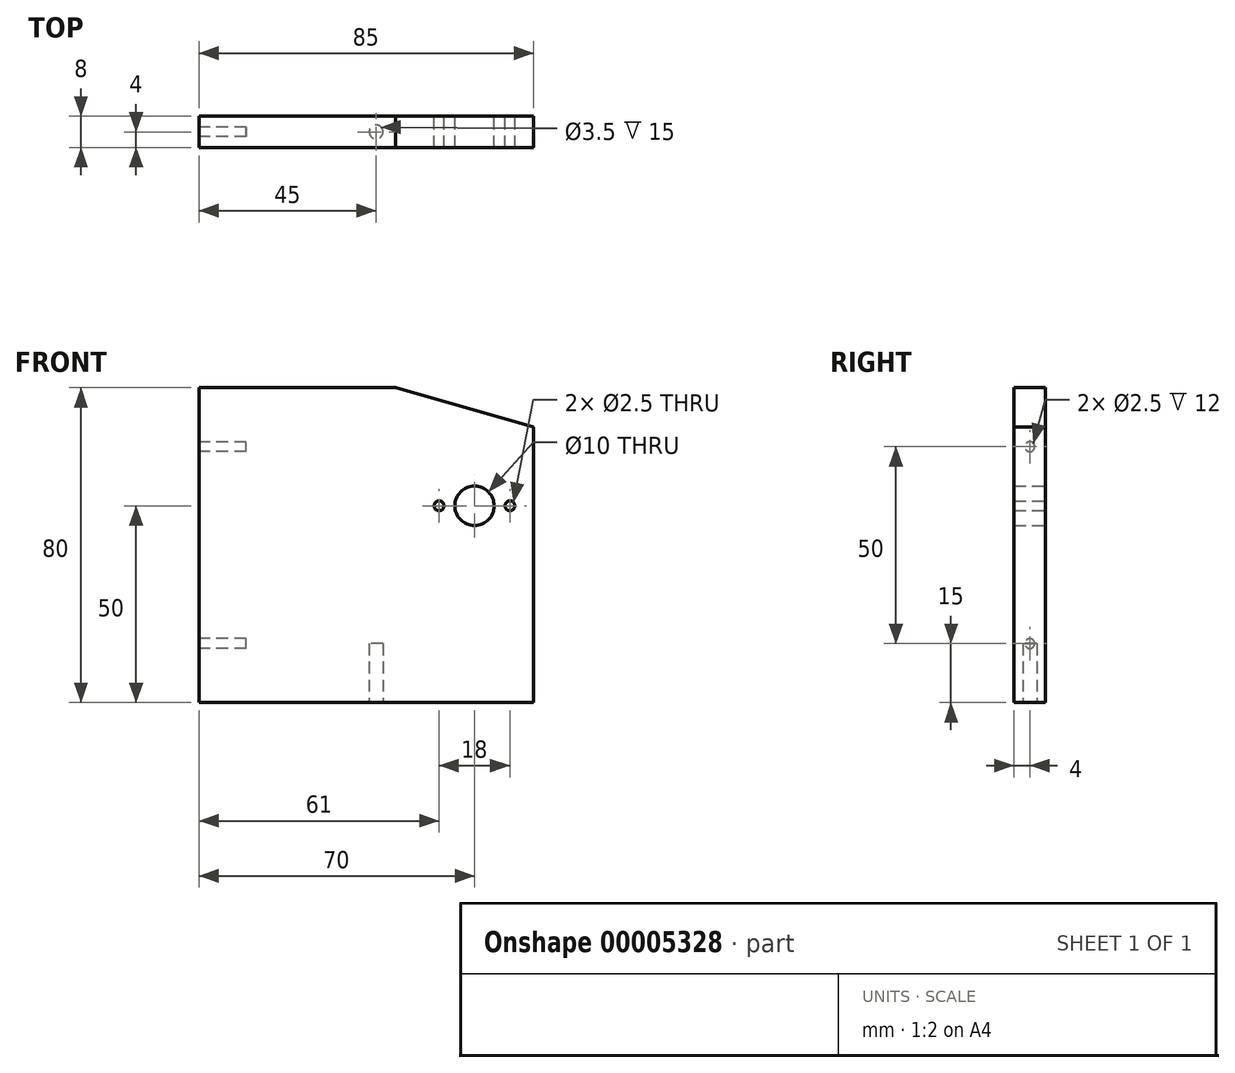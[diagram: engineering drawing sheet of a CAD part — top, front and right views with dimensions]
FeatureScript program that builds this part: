
annotation { "Feature Type Name" : "Feature", "Feature Type Description" : "" }
export const myFeature = defineFeature(function(context is Context, id is Id, definition is map)
    precondition{}
    {
        {
            var Q0;
            Q0=qCreatedBy(makeId("Front.planeOp"),FACE);
            var sketch = newSketch(context, id + "F0", { "sketchPlane" : qUnion([Q0])});
            skLineSegment(sketch, "E0.bottom", {"start": v(0, 0) * mm, "end": v(85, 0) * mm});
            skLineSegment(sketch, "E0.top", {"start": v(0, 80) * mm, "end": v(85, 80) * mm});
            skLineSegment(sketch, "E0.left", {"start": v(0, 0) * mm, "end": v(0, 80) * mm});
            skLineSegment(sketch, "E0.right", {"start": v(85, 0) * mm, "end": v(85, 80) * mm});
            skCircle(sketch, "E1", {"center": v(70, 50) * mm, "radius": 5 * mm});
            skLineSegment(sketch, "E2", {"start": v(89.38, 50) * mm, "end": v(49.05, 50) * mm});
            skCircle(sketch, "E3", {"center": v(61, 50) * mm, "radius": 1.25 * mm});
            skCircle(sketch, "E4", {"center": v(79, 50) * mm, "radius": 1.25 * mm});
            skLineSegment(sketch, "E5", {"start": v(50, 80) * mm, "end": v(85, 70) * mm});
            skSolve(sketch);
        }
        {
            var Q0;
            {var subQ13=sQuery(id+"F0.wireOp",EDGE,"E0.bottom");Q0=makeQuery(id+"F0.imprint","IMPRINT",FACE,{"disambiguationData":[TD([[makeQuery(id+"F0.imprint","IMPRINT",EDGE,{"derivedFrom":subQ13}),1.0]])]});}
            extrude(context, id + "F1", {"entities" : qUnion([Q0]), "depth" : 8 * mm});
        }
        {
            var Q0;
            Q0=qCreatedBy(makeId("Right.planeOp"),FACE);
            var sketch = newSketch(context, id + "F2", { "sketchPlane" : qUnion([Q0])});
            skLineSegment(sketch, "E6", {"start": v(-4, 73.45) * mm, "end": v(-4, 2.27) * mm});
            skCircle(sketch, "E7", {"center": v(-4, 15) * mm, "radius": 1.25 * mm});
            skCircle(sketch, "E8", {"center": v(-4, 65) * mm, "radius": 1.25 * mm});
            skSolve(sketch);
        }
        {
            var Q0;
            {var subQ0=sQuery(id+"F2.wireOp",EDGE,"E8");var subQ1=sQuery(id+"F2.wireOp",EDGE,"E6");var subQ3=makeQuery(id+"F2.imprint","INTERSECT",VERTEX,{"disambiguationData":[OD(0.0)],"derivedFrom":[subQ1,subQ0]});Q0=makeQuery(id+"F2.imprint","IMPRINT",FACE,{"disambiguationData":[TD([[makeQuery(id+"F2.imprint","IMPRINT",EDGE,{"disambiguationData":[TD([[subQ3,1.0]])],"derivedFrom":subQ1}),1.0]])]});}
            var Q1;
            {var subQ0=sQuery(id+"F2.wireOp",EDGE,"E8");var subQ1=sQuery(id+"F2.wireOp",EDGE,"E6");var subQ3=makeQuery(id+"F2.imprint","INTERSECT",VERTEX,{"disambiguationData":[OD(0.0)],"derivedFrom":[subQ1,subQ0]});Q1=makeQuery(id+"F2.imprint","IMPRINT",FACE,{"disambiguationData":[TD([[makeQuery(id+"F2.imprint","IMPRINT",EDGE,{"disambiguationData":[TD([[subQ3,1.0]])],"derivedFrom":subQ1}),-1.0]])]});}
            var Q2;
            {var subQ0=sQuery(id+"F2.wireOp",EDGE,"E7");var subQ1=sQuery(id+"F2.wireOp",EDGE,"E6");var subQ3=makeQuery(id+"F2.imprint","INTERSECT",VERTEX,{"disambiguationData":[OD(0.0)],"derivedFrom":[subQ1,subQ0]});Q2=makeQuery(id+"F2.imprint","IMPRINT",FACE,{"disambiguationData":[TD([[makeQuery(id+"F2.imprint","IMPRINT",EDGE,{"disambiguationData":[TD([[subQ3,1.0]])],"derivedFrom":subQ1}),1.0]])]});}
            var Q3;
            {var subQ0=sQuery(id+"F2.wireOp",EDGE,"E7");var subQ1=sQuery(id+"F2.wireOp",EDGE,"E6");var subQ3=makeQuery(id+"F2.imprint","INTERSECT",VERTEX,{"disambiguationData":[OD(0.0)],"derivedFrom":[subQ1,subQ0]});Q3=makeQuery(id+"F2.imprint","IMPRINT",FACE,{"disambiguationData":[TD([[makeQuery(id+"F2.imprint","IMPRINT",EDGE,{"disambiguationData":[TD([[subQ3,1.0]])],"derivedFrom":subQ1}),-1.0]])]});}
            extrude(context, id + "F3", {"entities" : qUnion([Q0, Q1, Q2, Q3]), "operationType" : NewBodyOperationType.REMOVE, "depth" : 12 * mm});
        }
        {
            var Q0;
            Q0=qCreatedBy(makeId("Top.planeOp"),FACE);
            var sketch = newSketch(context, id + "F4", { "sketchPlane" : qUnion([Q0])});
            skCircle(sketch, "E9", {"center": v(45, -4) * mm, "radius": 1.75 * mm});
            skSolve(sketch);
        }
        {
            var Q0;
            Q0=makeQuery(id+"F4.imprint","IMPRINT",FACE,{"disambiguationData":[TD([[makeQuery(id+"F4.imprint","IMPRINT",EDGE,{"derivedFrom":sQuery(id+"F4.wireOp",EDGE,"E9")}),1.0]])]});
            extrude(context, id + "F5", {"entities" : qUnion([Q0]), "operationType" : NewBodyOperationType.REMOVE, "depth" : 15 * mm});
        }
    });
